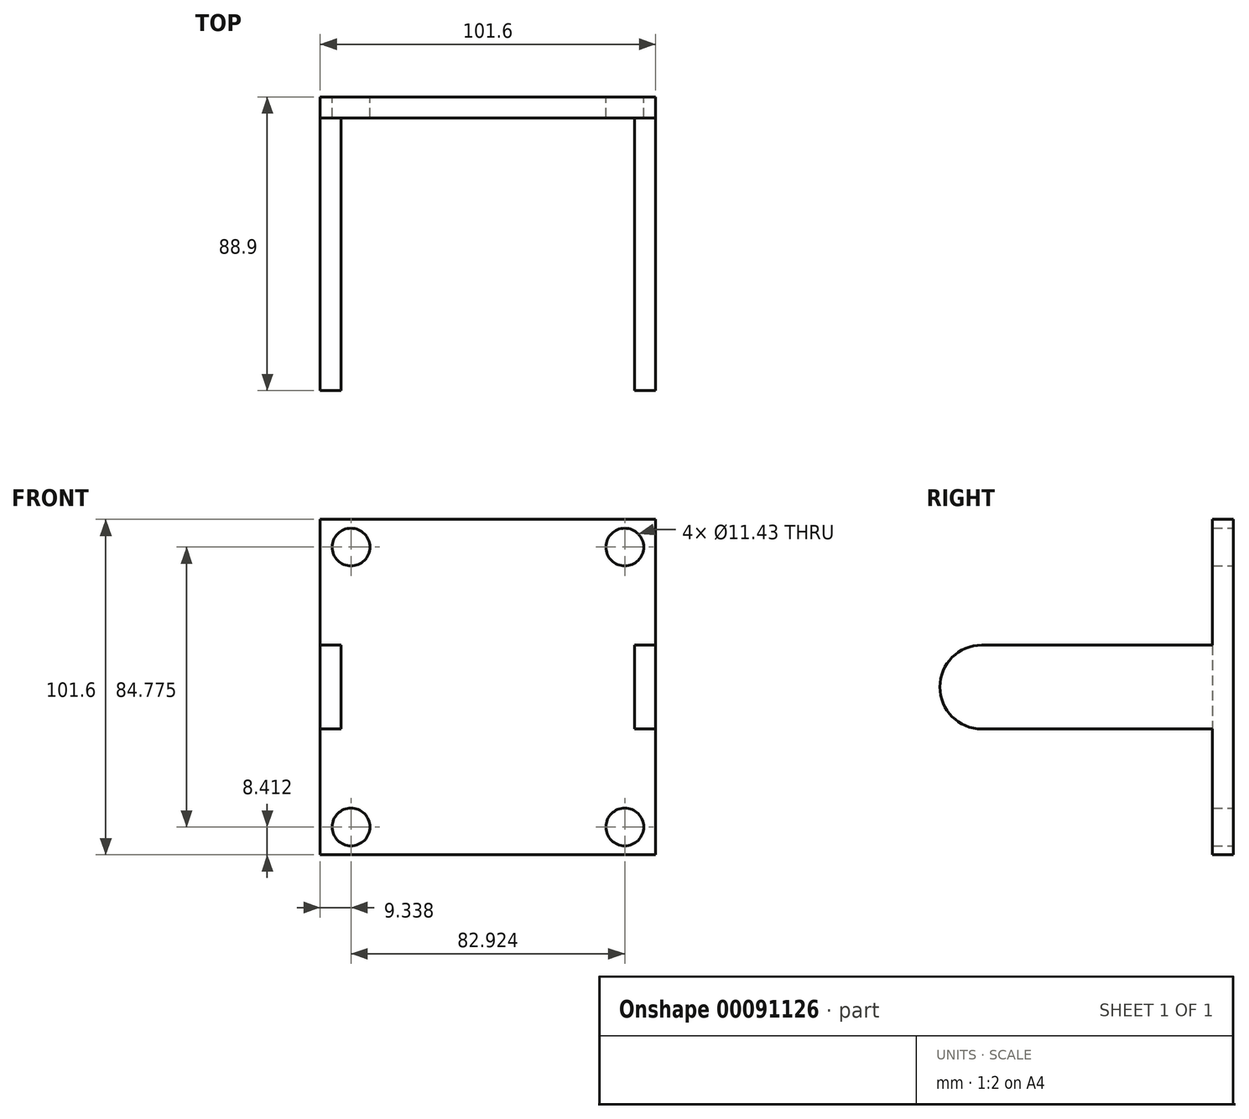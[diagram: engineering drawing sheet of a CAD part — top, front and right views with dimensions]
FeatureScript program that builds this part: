
annotation { "Feature Type Name" : "Feature", "Feature Type Description" : "" }
export const myFeature = defineFeature(function(context is Context, id is Id, definition is map)
    precondition{}
    {
        {
            var Q0;
            Q0=qCreatedBy(makeId("Front.planeOp"),FACE);
            var sketch = newSketch(context, id + "F0", { "sketchPlane" : qUnion([Q0])});
            skLineSegment(sketch, "E0.bottom", {"start": v(50.8, 50.8) * mm, "end": v(-50.8, 50.8) * mm});
            skLineSegment(sketch, "E0.top", {"start": v(50.8, -50.8) * mm, "end": v(-50.8, -50.8) * mm});
            skLineSegment(sketch, "E0.left", {"start": v(50.8, 50.8) * mm, "end": v(50.8, -50.8) * mm});
            skLineSegment(sketch, "E0.right", {"start": v(-50.8, 50.8) * mm, "end": v(-50.8, -50.8) * mm});
            skSolve(sketch);
        }
        {
            var Q0;
            Q0=makeQuery(id+"F0.imprint","IMPRINT",FACE,{"disambiguationData":[TD([[makeQuery(id+"F0.imprint","IMPRINT",EDGE,{"derivedFrom":sQuery(id+"F0.wireOp",EDGE,"E0.bottom")}),1.0]])]});
            extrude(context, id + "F1", {"entities" : qUnion([Q0]), "depth" : 6.35 * mm});
        }
        {
            var Q0;
            Q0=qCreatedBy(makeId("Front.planeOp"),FACE);
            var sketch = newSketch(context, id + "F2", { "sketchPlane" : qUnion([Q0])});
            skCircle(sketch, "E1", {"center": v(-41.46, 42.39) * mm, "radius": 5.72 * mm});
            skCircle(sketch, "E2.MirrorC", {"center": v(41.46, 42.39) * mm, "radius": 5.72 * mm});
            skCircle(sketch, "E3.MirrorC", {"center": v(-41.46, -42.39) * mm, "radius": 5.72 * mm});
            skCircle(sketch, "E4.MirrorC", {"center": v(41.46, -42.39) * mm, "radius": 5.72 * mm});
            skSolve(sketch);
        }
        {
            var Q0;
            Q0 = qSketchRegion(id + "F2", true);
            extrude(context, id + "F3", {"entities" : qUnion([Q0]), "operationType" : NewBodyOperationType.REMOVE, "depth" : 6.35 * mm});
        }
        {
            var Q0;
            Q0=makeQuery(id+"F1.opExtrude","SWEPT_FACE",FACE,{"disambiguationData":[OSD([sQuery(id+"F0.wireOp",EDGE,"E0.right")])]});
            cPlane(context, id + "F4", {"entities" : qUnion([Q0]), "cplaneType" : CPlaneType.OFFSET, "offset" : 0 * mm, "width" : 152.4 * mm, "height" : 152.4 * mm});
        }
        {
            var Q0;
            Q0=qCreatedBy(id+"F4.planeOp",FACE);
            var sketch = newSketch(context, id + "F5", { "sketchPlane" : qUnion([Q0])});
            skLineSegment(sketch, "E5.bottom", {"start": v(0, 12.7) * mm, "end": v(76.2, 12.7) * mm});
            skLineSegment(sketch, "E5.top", {"start": v(0, -12.7) * mm, "end": v(76.2, -12.7) * mm});
            skLineSegment(sketch, "E5.left", {"start": v(0, 12.7) * mm, "end": v(0, -12.7) * mm});
            skArc(sketch, "E6", {"start": v(76.2, 12.7) * mm, "mid": v(88.9, 0) * mm, "end": v(76.2, -12.7) * mm});
            skSolve(sketch);
        }
        {
            var Q0;
            Q0=makeQuery(id+"F1.opExtrude","SWEPT_FACE",FACE,{"disambiguationData":[OSD([sQuery(id+"F0.wireOp",EDGE,"E0.left")])]});
            cPlane(context, id + "F6", {"entities" : qUnion([Q0]), "cplaneType" : CPlaneType.OFFSET, "offset" : 0 * mm, "width" : 152.4 * mm, "height" : 152.4 * mm});
        }
        {
            var Q0;
            Q0=qCreatedBy(id+"F6.planeOp",FACE);
            var sketch = newSketch(context, id + "F7", { "sketchPlane" : qUnion([Q0])});
            skLineSegment(sketch, "E7.bottom", {"start": v(0, 12.7) * mm, "end": v(-76.2, 12.7) * mm});
            skLineSegment(sketch, "E7.top", {"start": v(0, -12.7) * mm, "end": v(-76.2, -12.7) * mm});
            skLineSegment(sketch, "E7.left", {"start": v(0, 12.7) * mm, "end": v(0, -12.7) * mm});
            skArc(sketch, "E8", {"start": v(-76.2, 12.7) * mm, "mid": v(-88.9, 0) * mm, "end": v(-76.2, -12.7) * mm});
            skSolve(sketch);
        }
        {
            var Q0;
            Q0 = qSketchRegion(id + "F7", true);
            extrude(context, id + "F8", {"entities" : qUnion([Q0]), "operationType" : NewBodyOperationType.ADD, "oppositeDirection" : true, "depth" : 6.35 * mm});
        }
        {
            var Q0;
            Q0 = qSketchRegion(id + "F5", true);
            extrude(context, id + "F9", {"entities" : qUnion([Q0]), "operationType" : NewBodyOperationType.ADD, "oppositeDirection" : true, "depth" : 6.35 * mm});
        }
    });
